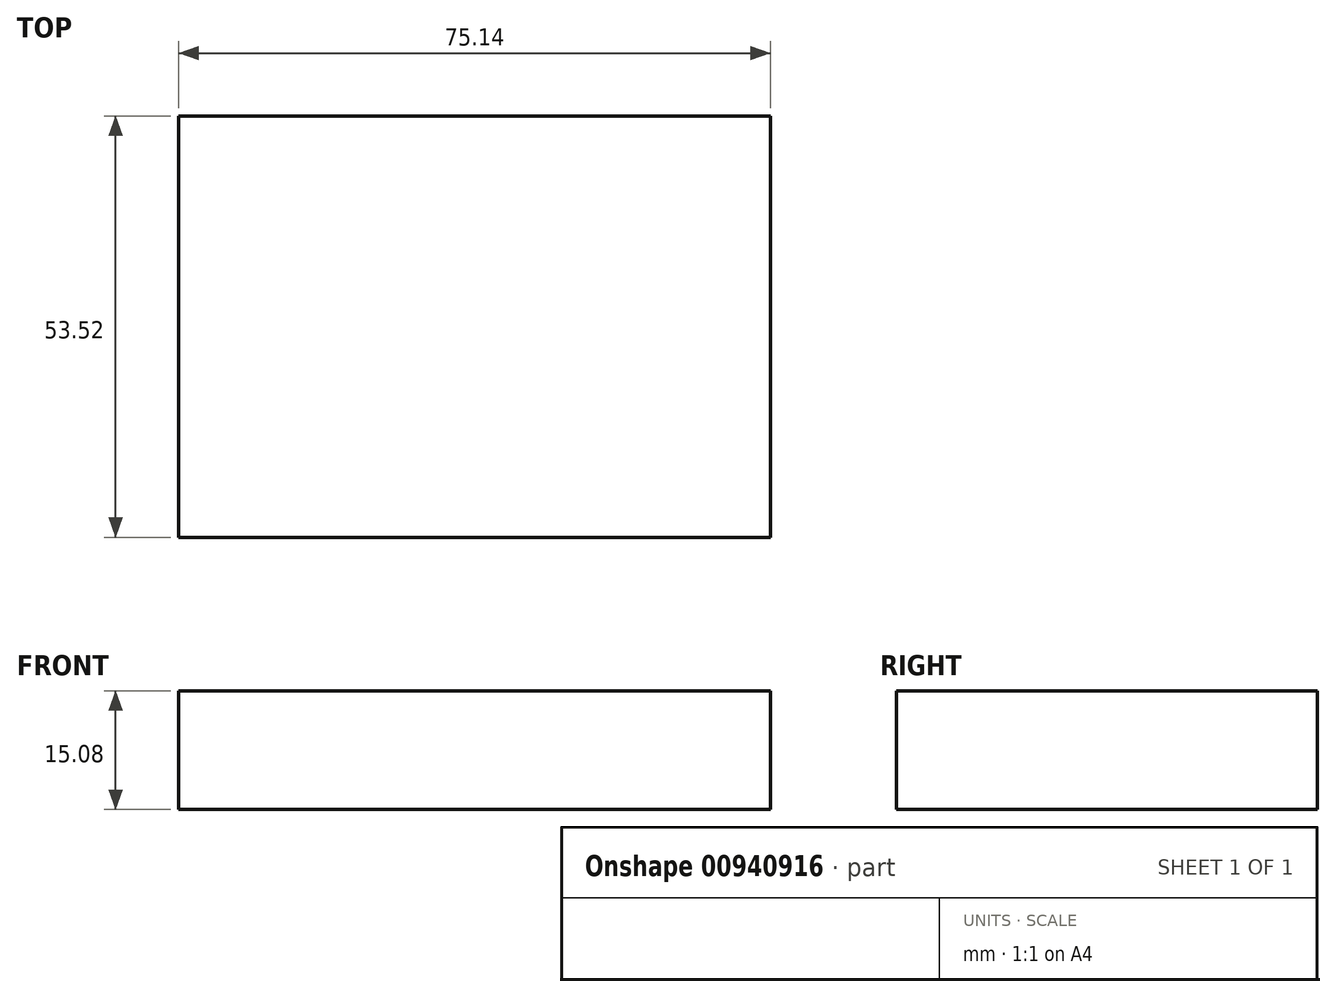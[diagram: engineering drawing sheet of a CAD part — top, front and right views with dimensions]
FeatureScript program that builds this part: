
annotation { "Feature Type Name" : "Feature", "Feature Type Description" : "" }
export const myFeature = defineFeature(function(context is Context, id is Id, definition is map)
    precondition{}
    {
        {
            var Q0;
            Q0=qCreatedBy(makeId("Top.planeOp"),FACE);
            var sketch = newSketch(context, id + "F0", { "sketchPlane" : qUnion([Q0])});
            skLineSegment(sketch, "E0.bottom", {"start": v(-37.57, 26.76) * mm, "end": v(37.57, 26.76) * mm});
            skLineSegment(sketch, "E0.top", {"start": v(-37.57, -26.76) * mm, "end": v(37.57, -26.76) * mm});
            skLineSegment(sketch, "E0.left", {"start": v(-37.57, 26.76) * mm, "end": v(-37.57, -26.76) * mm});
            skLineSegment(sketch, "E0.right", {"start": v(37.57, 26.76) * mm, "end": v(37.57, -26.76) * mm});
            skPoint(sketch, "E0.middle", {"position": v(0, 0) * mm});
            skSolve(sketch);
        }
        {
            var Q0;
            Q0=makeQuery(id+"F0.imprint","IMPRINT",FACE,{"disambiguationData":[TD([[makeQuery(id+"F0.imprint","IMPRINT",EDGE,{"derivedFrom":sQuery(id+"F0.wireOp",EDGE,"E0.bottom")}),-1.0]])]});
            extrude(context, id + "F1", {"entities" : qUnion([Q0]), "oppositeDirection" : true, "depth" : 15.08 * mm, "offsetDistance" : 25 * mm});
        }
    });
